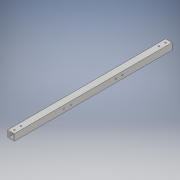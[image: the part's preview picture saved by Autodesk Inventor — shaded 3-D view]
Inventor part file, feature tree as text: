
AUTODESK INVENTOR PART (.ipt)
format: ipt  version: 2018 (Build 220112000, 112)  size: 135,168 bytes
history: native  units: in
note: dims shown in document units (in); Inventor stores cm internally (conversion verified against a paired STEP export)
features: extrude x3, sketch x3
ambient origin geometry x8: Origin, YZ Plane, XZ Plane, XY Plane, X Axis, Y Axis, Z Axis, Center Point
bodies: Solid1 (feature_tree)
feature tree (6):
  extrude  "Extrusion1"  Depth=1.0in
  extrude  "Extrusion2"  Depth=24.0in TaperAngle=0.0deg
  extrude  "Extrusion3"  Depth=1.0in
  sketch  "Sketch1"  dims[d0=1.0in d1=1.0in]
  sketch  "Sketch2"  dims[d2=0.125in d3=24.0in d4=0.0in]
  sketch  "Sketch3"  dims[d5=0.5in d6=1.0in d7=0.2031in d8=24.0in d9=0.0in d10=3.937in d11=0.5in d12=1.0in d13=0.2031in d14=1.0in d15=0.0in]
